# Revit family: Faucet-Wall_Mount-Lavatory-KOHLER-ALEO-K-25106T_1
name_source: partatom
category: Plumbing Fixtures
units: mm (PartAtom-declared; Revit-internal decimal feet)

## family parameters
Cut with Voids When Loaded = No
Host = Face
Maintain Annotation Orientation = No
OmniClass Number = 23.31.11.00
OmniClass Title = Faucets
Part Type = Normal
Room Calculation Point = No
Round Connector Dimension = Use Diameter
Shared = No

## types (4) — shared parameters
ADA Compliant = No
Assembly Code = D2010
CW Connection = Yes
Cold Water Inlet = Cold Water Inlet
Date Modified = 03/28/2022
Default Elevation = 36"
Drain Included = Yes
Flow Rate = 2 GPM
HW Connection = Yes
Handle Clearance = 3 3/8"
Hot Water Inlet = Hot Water Inlet
Length = 8 9/16"
Manufacturer = KOHLER Co.
Master Format 2014 = 22 41 39
Master Format 2014 Name = Residential Faucets, Supplies, and Trim
Material = Premium Metal Construction
Pressure = 60.00 psi
Product Name = ALEO
Spout Reach = 8 9/16"
URL = http://www.kohler.com.cn
Vent Connection = No
Waste Connection = No
Waste Water Outlet = Waste Water Outlet
WaterSense Certified = No
Width = 4"

## per-type parameters (varying)
| type | Description | Distance | Finish | Height | Model | Product Documentation Link | Product Page URL | Type | Valve |
| With Valve, CP-Polished Chrome | Single-handle wall outlet basin faucet | 2 15/16" | Kohler-Metal-CP-Polished_Chrome | 2 5/16" | K-25106T-4-CP | https://files.kohler.com.cn | https://www.kohler.com.cn | 1 | Yes |
| With Valve, 2BL-Original Black | Single-handle wall outlet basin faucet | 2 15/16" | Kohler-Metal-2BL-Original_Black | 2 5/16" | K-25106T-4-2BL | https://files.kohler.com.cn | https://www.kohler.com.cn | 2 | Yes |
| Without Valve, CP-Polished Chrome | Single Handle Wall Mount Lavatory Faucet Without Valve | 0" | Kohler-Metal-CP-Polished_Chrome | 2 9/16" | K-25106T-B4-CP |  |  | 3 | No |
| Without Valve, BL-Matte Black | Single Handle Wall Mount Lavatory Faucet Without Valve | 0" | Kohler-Metal-BL-Matte_Black | 2 9/16" | K-25106T-B4-BL |  |  | 4 | No |

## geometry (parser evidence)
native form markers: Sweep x5
no freeform markers — native parametric forms only
